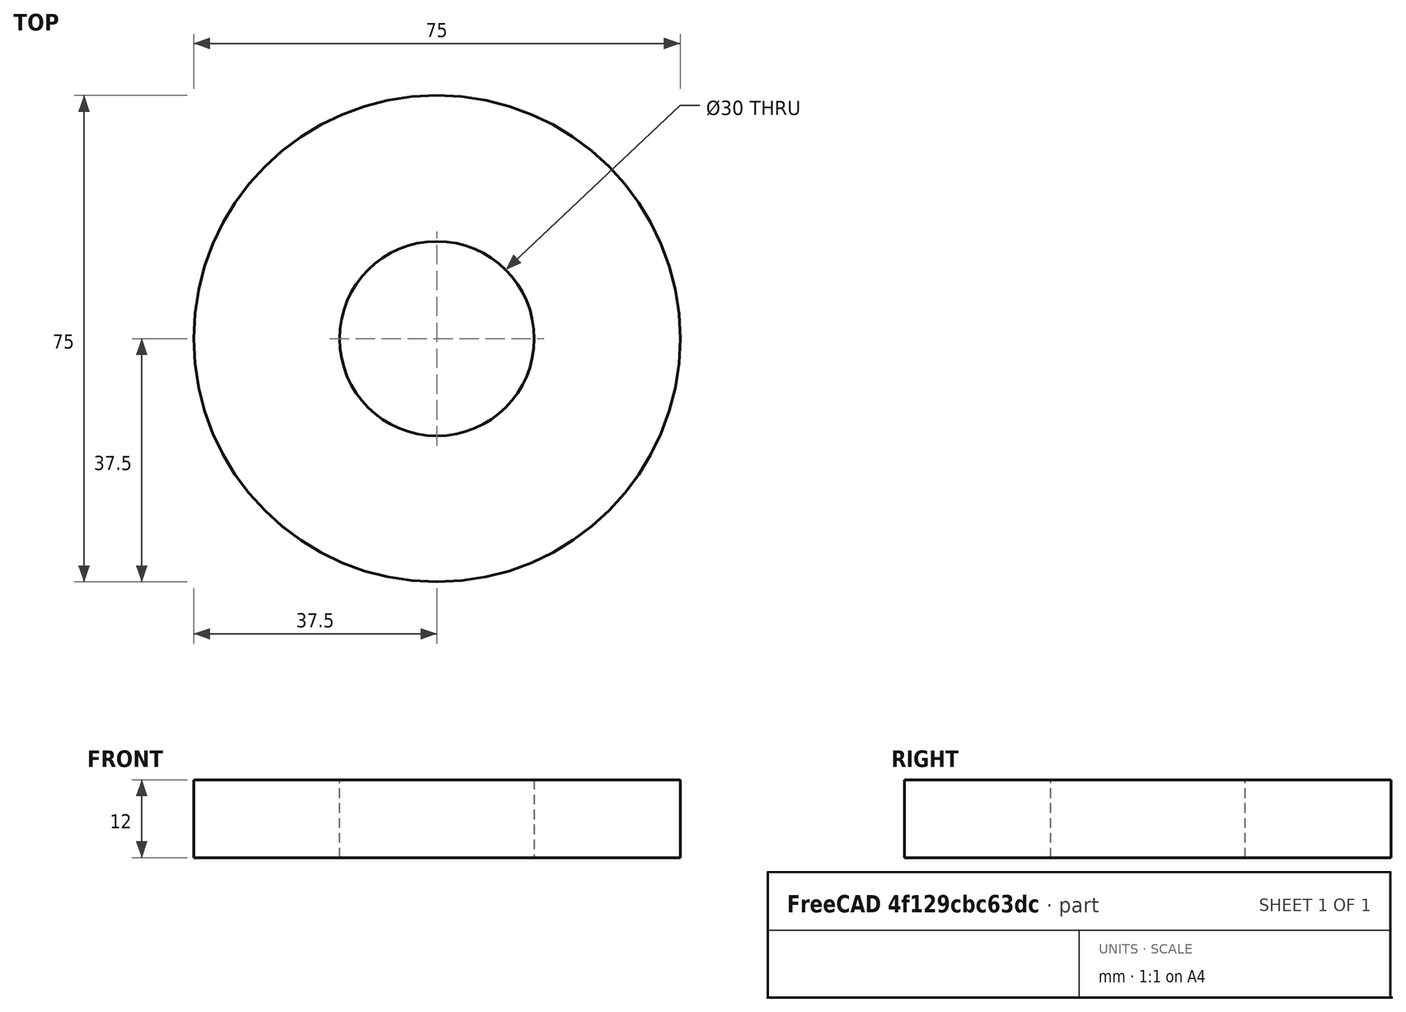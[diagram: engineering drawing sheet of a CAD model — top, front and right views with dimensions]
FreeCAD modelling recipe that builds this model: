
FCSTD DOCUMENT  (FreeCAD 1.0R39319 (Git))
Label: Espacador_BTP_75x30x12
License: All rights reserved
LicenseURL: https://en.wikipedia.org/wiki/All_rights_reserved
objects: Sketcher::SketchObject×2, PartDesign::Pad×1, PartDesign::Pocket×1, PartDesign::Body×1
note: 11 computed .brp shape members not serialized (recipe doc carries the construction recipe); baked Part::Feature solids carry a one-line shape summary decoded from their .brp

FEATURE [Sketcher::SketchObject] Sketch_1
  ArcFitTolerance = 1e-06
  AttachmentSupport = -> [XY_Plane]
  FullyConstrained = false
  MakeInternals = false
  MapMode = 5
  sketch-geometry (1):
    g0: Circle CenterX=0 CenterY=0 CenterZ=0 NormalX=0 NormalY=0 NormalZ=1 AngleXU=0 Radius=37.5
FEATURE [PartDesign::Pad] Pad_1
  Direction = (0,0,1)
  Length = 12
  Length2 = 10
  Profile = -> Sketch_1
  Refine = true
  Suppressed = false
  Type = 0
FEATURE [Sketcher::SketchObject] Sketch_2
  ArcFitTolerance = 1e-06
  AttachmentSupport = -> [Pad_1]
  FullyConstrained = false
  MakeInternals = false
  MapMode = 5
  Placement = pos=(0,0,12) rot=(0,0,1;0rad)
  sketch-geometry (1):
    g0: Circle CenterX=0 CenterY=0 CenterZ=0 NormalX=0 NormalY=0 NormalZ=1 AngleXU=0 Radius=15
FEATURE [PartDesign::Pocket] Pocket_2
  BaseFeature = -> Pad_1
  Direction = (0,0,-1)
  Length = 5
  Length2 = 5
  Profile = -> Sketch_2
  Refine = true
  Suppressed = false
  Type = 1
FEATURE [PartDesign::Body] Body
  AllowCompound = false
  Group = -> [Sketch_1,Pad_1,Sketch_2,Pocket_2]
  Origin = -> Origin
  Tip = -> Pocket_2
